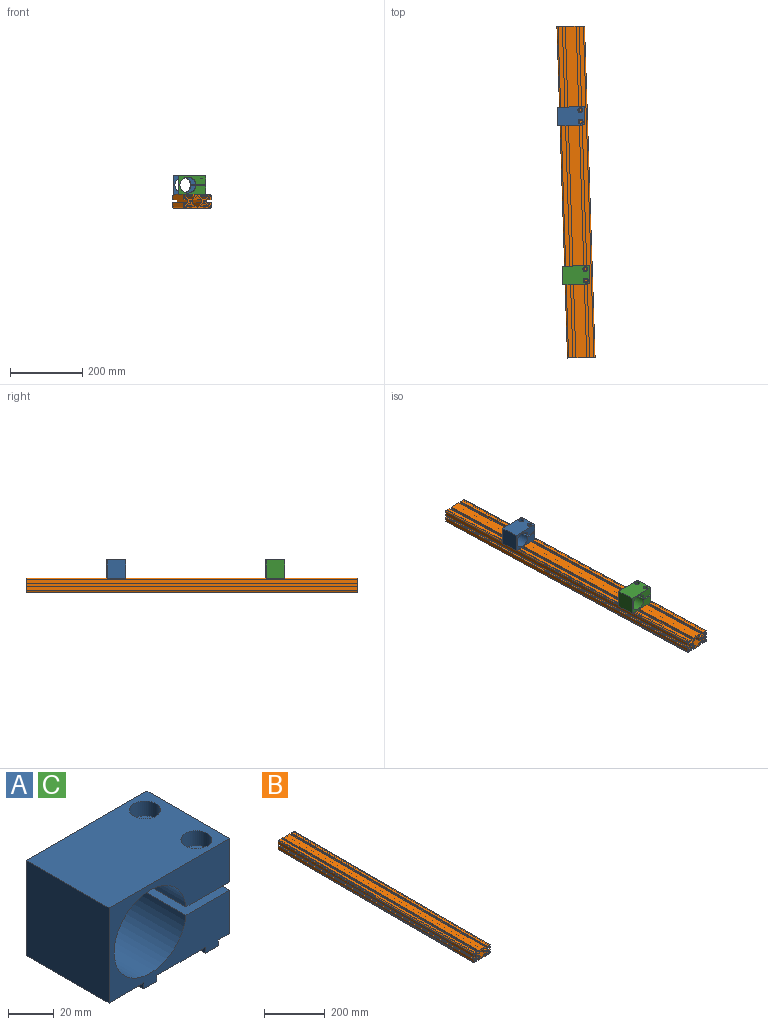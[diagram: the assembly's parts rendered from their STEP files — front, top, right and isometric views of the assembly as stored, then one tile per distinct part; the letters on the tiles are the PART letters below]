
ASSEMBLY  parts=3 mates=4
PART A: 32 faces, bbox 74.3x50.8x54 mm
  f0: plane 29.16x3.18mm, normal (-1,0,0), area 92.6mm2, adj f4,f13,f30,f31
  f1: plane 8.23x3.18mm, normal (-1,0,0), area 26.1mm2, adj f3,f13,f23,f31
  f2: plane 8.23x3.18mm, normal (-1,0,0), area 26.1mm2, adj f13,f14,f22,f30
  f3: plane 8.23x8.03mm, normal (0,0,-1), area 48.9mm2, adj f1,f5,f23,f31
  f4: plane 29.16x8.03mm, normal (0,0,-1), area 199.7mm2, adj f0,f6,f30,f31
  f5: plane 8.23x3.18mm, normal (1,0,0), area 26.1mm2, adj f3,f15,f23,f31
  f6: plane 29.16x3.18mm, normal (1,0,0), area 92.6mm2, adj f4,f15,f30,f31
  f7: plane 8.23x3.18mm, normal (1,0,0), area 26.1mm2, adj f14,f15,f22,f30
  f8: plane 50.8x50.8mm, normal (-1,0,0), area 2580.6mm2, adj f9,f21,f22,f23
  f9: plane 50.8x21.39mm, normal (0,0,-1), area 1086.4mm2, adj f8,f10,f22,f23
  f10: plane 50.8x3.18mm, normal (-1,0,0), area 161.3mm2, adj f9,f11,f22,f23
  f11: plane 50.8x8.03mm, normal (0,0,-1), area 407.7mm2, adj f10,f12,f22,f23
  f12: plane 50.8x3.18mm, normal (1,0,0), area 161.3mm2, adj f11,f13,f22,f23
  f13: plane 50.8x30.07mm, normal (0,0,-1), area 1527mm2, adj f0,f1,f2,f12,f22,f23,f30,f31
  f14: plane 8.23x8.03mm, normal (0,0,-1), area 48.9mm2, adj f2,f7,f22,f30
  f15: plane 50.8x6.74mm, normal (0,0,-1), area 341.6mm2, adj f5,f6,f7,f16,f22,f23,f30,f31
  f16: plane 50.8x23.18mm, normal (1,0,0), area 1177.4mm2, adj f15,f17,f22,f23
  f17: plane 50.8x26.74mm, normal (0,0,1), area 1246.5mm2, adj f16,f18,f22,f23,f30,f31
  f18: cylinder r=22.23mm len=50.8mm, axis (0,-1,0), area 6867.7mm2, adj f17,f19,f22,f23
  f19: plane 50.8x26.74mm, normal (0,0,-1), area 1246.5mm2, adj f18,f20,f22,f23,f24,f27
  f20: plane 50.8x23.18mm, normal (1,0,0), area 1177.4mm2, adj f19,f21,f22,f23
  f21: plane 74.25x50.8mm, normal (0,0,1), area 3485.9mm2, adj f8,f20,f22,f23,f26,f29
  f22: plane 74.25x53.98mm, normal (0,1,0), area 2152.6mm2, adj f2,f7,f8,f9,f10,f11,f12,f13
  f23: plane 74.25x53.98mm, normal (0,-1,0), area 2152.6mm2, adj f1,f3,f5,f8,f9,f10,f11,f12
  f24: cylinder r=4.22mm len=15.24mm, axis (0,0,1), area 403.7mm2, adj f19,f25
  f25: plane 13.49x13.49mm, normal (0,0,1), area 87.2mm2, adj f24,f26
  f26: cylinder r=6.75mm len=13.49mm, axis (0,0,1), area 336.5mm2, adj f21,f25
  f27: cylinder r=4.22mm len=15.24mm, axis (0,0,1), area 403.7mm2, adj f19,f28
  f28: plane 13.49x13.49mm, normal (0,0,1), area 87.2mm2, adj f27,f29
  f29: cylinder r=6.75mm len=13.49mm, axis (0,0,1), area 336.5mm2, adj f21,f28
  f30: cylinder r=4.22mm len=26.35mm, axis (0,0,1), area 681.4mm2, adj f0,f2,f4,f6,f7,f13,f14,f15
  f31: cylinder r=4.22mm len=26.35mm, axis (0,0,1), area 681.4mm2, adj f0,f1,f3,f4,f5,f6,f13,f15
PART B: 122 faces, bbox 76.2x914.4x38.1 mm
  f0: plane 76.2x38.1mm, normal (0,-1,0), area 1182.5mm2, adj f2,f3,f4,f5,f6,f7,f8,f9
  f1: plane 76.2x38.1mm, normal (0,1,0), area 1182.5mm2, adj f2,f3,f4,f5,f6,f7,f8,f9
  f2: plane 914.4x5.71mm, normal (0.71,0,0.71), area 7385.6mm2, adj f0,f1,f3,f93
  f3: plane 914.4x3.23mm, normal (1,0,0), area 2953.1mm2, adj f0,f1,f2,f4
  f4: plane 914.4x3.43mm, normal (0,0,-1), area 3135.5mm2, adj f0,f1,f3,f5
  f5: plane 914.4x1.17mm, normal (-1,0,0), area 1068.4mm2, adj f0,f1,f4,f6
  f6: plane 914.4x2.79mm, normal (0,0,-1), area 2554.8mm2, adj f0,f1,f5,f7
  f7: plane 914.4x4.55mm, normal (1,0,0), area 4157.4mm2, adj f0,f1,f6,f8
  f8: plane 914.4x11.94mm, normal (0,0,1), area 10916.1mm2, adj f0,f1,f7,f9
  f9: cylinder r=3.05mm len=914.4mm, axis (0,1,0), area 4378mm2, adj f0,f1,f8,f10
  f10: plane 914.4x11.94mm, normal (-1,0,0), area 10916.1mm2, adj f0,f1,f9,f11
  f11: plane 914.4x4.55mm, normal (0,0,-1), area 4157.4mm2, adj f0,f1,f10,f12
  f12: plane 914.4x2.79mm, normal (1,0,0), area 2554.8mm2, adj f0,f1,f11,f13
  f13: plane 914.4x1.17mm, normal (0,0,1), area 1068.4mm2, adj f0,f1,f12,f14
  f14: plane 914.4x3.43mm, normal (1,0,0), area 3135.5mm2, adj f0,f1,f13,f15
  f15: plane 914.4x3.23mm, normal (0,0,-1), area 2953.1mm2, adj f0,f1,f14,f16
  f16: plane 914.4x5.71mm, normal (-0.71,0,-0.71), area 7385.6mm2, adj f0,f1,f15,f17
  f17: plane 914.4x9.15mm, normal (-1,0,0), area 8368.1mm2, adj f0,f1,f16,f18
  f18: plane 914.4x5.71mm, normal (-0.71,0,0.71), area 7385.6mm2, adj f0,f1,f17,f19
  f19: plane 914.4x3.23mm, normal (0,0,1), area 2953.1mm2, adj f0,f1,f18,f20
  f20: plane 914.4x3.43mm, normal (1,0,0), area 3135.5mm2, adj f0,f1,f19,f21
  f21: plane 914.4x1.17mm, normal (0,0,-1), area 1068.4mm2, adj f0,f1,f20,f22
  f22: plane 914.4x2.79mm, normal (1,0,0), area 2554.8mm2, adj f0,f1,f21,f23
  f23: plane 914.4x4.55mm, normal (0,0,1), area 4157.4mm2, adj f0,f1,f22,f24
  f24: plane 914.4x11.94mm, normal (-1,0,0), area 10916.1mm2, adj f0,f1,f23,f25
  f25: cylinder r=3.05mm len=914.4mm, axis (0,1,0), area 4378mm2, adj f0,f1,f24,f26
  f26: plane 914.4x11.94mm, normal (0,0,-1), area 10916.1mm2, adj f0,f1,f25,f27
  f27: plane 914.4x4.55mm, normal (1,0,0), area 4157.4mm2, adj f0,f1,f26,f28
  f28: plane 914.4x2.79mm, normal (0,0,1), area 2554.8mm2, adj f0,f1,f27,f29
  f29: plane 914.4x1.17mm, normal (-1,0,0), area 1068.4mm2, adj f0,f1,f28,f30
  f30: plane 914.4x3.43mm, normal (0,0,1), area 3135.5mm2, adj f0,f1,f29,f31
  f31: plane 914.4x3.23mm, normal (1,0,0), area 2953.1mm2, adj f0,f1,f30,f32
  f32: plane 914.4x5.71mm, normal (0.71,0,-0.71), area 7385.6mm2, adj f0,f1,f31,f33
  f33: plane 914.4x9.15mm, normal (0,0,-1), area 8368.1mm2, adj f0,f1,f32,f34
  f34: plane 914.4x5.71mm, normal (-0.71,0,-0.71), area 7385.6mm2, adj f0,f1,f33,f35
  f35: plane 914.4x3.23mm, normal (-1,0,0), area 2953.1mm2, adj f0,f1,f34,f36
  f36: plane 914.4x3.43mm, normal (0,0,1), area 3135.5mm2, adj f0,f1,f35,f37
  f37: plane 914.4x1.17mm, normal (1,0,0), area 1068.4mm2, adj f0,f1,f36,f38
  f38: plane 914.4x2.79mm, normal (0,0,1), area 2554.8mm2, adj f0,f1,f37,f39
  f39: plane 914.4x4.55mm, normal (-1,0,0), area 4157.4mm2, adj f0,f1,f38,f40
  f40: plane 914.4x29.97mm, normal (0,0,-1), area 27406.4mm2, adj f0,f1,f39,f41
  f41: plane 914.4x4.55mm, normal (1,0,0), area 4157.4mm2, adj f0,f1,f40,f42
  f42: plane 914.4x2.79mm, normal (0,0,1), area 2554.8mm2, adj f0,f1,f41,f43
  f43: plane 914.4x1.17mm, normal (-1,0,0), area 1068.4mm2, adj f0,f1,f42,f44
  f44: plane 914.4x3.43mm, normal (0,0,1), area 3135.5mm2, adj f0,f1,f43,f45
  f45: plane 914.4x3.23mm, normal (1,0,0), area 2953.1mm2, adj f0,f1,f44,f46
  f46: plane 914.4x5.71mm, normal (0.71,0,-0.71), area 7385.6mm2, adj f0,f1,f45,f47
  f47: plane 914.4x9.15mm, normal (0,0,-1), area 8368.1mm2, adj f0,f1,f46,f48
  f48: plane 914.4x5.71mm, normal (-0.71,0,-0.71), area 7385.6mm2, adj f0,f1,f47,f49
  f49: plane 914.4x3.23mm, normal (-1,0,0), area 2953.1mm2, adj f0,f1,f48,f50
  f50: plane 914.4x3.43mm, normal (0,0,1), area 3135.5mm2, adj f0,f1,f49,f51
  f51: plane 914.4x1.17mm, normal (1,0,0), area 1068.4mm2, adj f0,f1,f50,f52
  f52: plane 914.4x2.79mm, normal (0,0,1), area 2554.8mm2, adj f0,f1,f51,f53
  f53: plane 914.4x4.55mm, normal (-1,0,0), area 4157.4mm2, adj f0,f1,f52,f54
  f54: plane 914.4x11.94mm, normal (0,0,-1), area 10916.1mm2, adj f0,f1,f53,f55
  f55: cylinder r=3.05mm len=914.4mm, axis (0,1,0), area 4378mm2, adj f0,f1,f54,f56
  f56: plane 914.4x11.94mm, normal (1,0,0), area 10916.1mm2, adj f0,f1,f55,f57
  f57: plane 914.4x4.55mm, normal (0,0,1), area 4157.4mm2, adj f0,f1,f56,f58
  f58: plane 914.4x2.79mm, normal (-1,0,0), area 2554.8mm2, adj f0,f1,f57,f59
  f59: plane 914.4x1.17mm, normal (0,0,-1), area 1068.4mm2, adj f0,f1,f58,f60
  f60: plane 914.4x3.43mm, normal (-1,0,0), area 3135.5mm2, adj f0,f1,f59,f61
  f61: plane 914.4x3.23mm, normal (0,0,1), area 2953.1mm2, adj f0,f1,f60,f62
  f62: plane 914.4x5.71mm, normal (0.71,0,0.71), area 7385.6mm2, adj f0,f1,f61,f63
  f63: plane 914.4x9.15mm, normal (1,0,0), area 8368.1mm2, adj f0,f1,f62,f64
  f64: plane 914.4x5.71mm, normal (0.71,0,-0.71), area 7385.6mm2, adj f0,f1,f63,f65
  f65: plane 914.4x3.23mm, normal (0,0,-1), area 2953.1mm2, adj f0,f1,f64,f66
  f66: plane 914.4x3.43mm, normal (-1,0,0), area 3135.5mm2, adj f0,f1,f65,f67
  f67: plane 914.4x1.17mm, normal (0,0,1), area 1068.4mm2, adj f0,f1,f66,f68
  f68: plane 914.4x2.79mm, normal (-1,0,0), area 2554.8mm2, adj f0,f1,f67,f69
  f69: plane 914.4x4.55mm, normal (0,0,-1), area 4157.4mm2, adj f0,f1,f68,f70
  f70: plane 914.4x11.94mm, normal (1,0,0), area 10916.1mm2, adj f0,f1,f69,f71
  f71: cylinder r=3.05mm len=914.4mm, axis (0,1,0), area 4378mm2, adj f0,f1,f70,f72
  f72: plane 914.4x11.94mm, normal (0,0,1), area 10916.1mm2, adj f0,f1,f71,f73
  f73: plane 914.4x4.55mm, normal (-1,0,0), area 4157.4mm2, adj f0,f1,f72,f74
  f74: plane 914.4x2.79mm, normal (0,0,-1), area 2554.8mm2, adj f0,f1,f73,f75
  f75: plane 914.4x1.17mm, normal (1,0,0), area 1068.4mm2, adj f0,f1,f74,f76
  f76: plane 914.4x3.43mm, normal (0,0,-1), area 3135.5mm2, adj f0,f1,f75,f77
  f77: plane 914.4x3.23mm, normal (-1,0,0), area 2953.1mm2, adj f0,f1,f76,f78
  f78: plane 914.4x5.71mm, normal (-0.71,0,0.71), area 7385.6mm2, adj f0,f1,f77,f79
  f79: plane 914.4x9.15mm, normal (0,0,1), area 8368.1mm2, adj f0,f1,f78,f80
  f80: plane 914.4x5.71mm, normal (0.71,0,0.71), area 7385.6mm2, adj f0,f1,f79,f81
  f81: plane 914.4x3.23mm, normal (1,0,0), area 2953.1mm2, adj f0,f1,f80,f82
  f82: plane 914.4x3.43mm, normal (0,0,-1), area 3135.5mm2, adj f0,f1,f81,f83
  f83: plane 914.4x1.17mm, normal (-1,0,0), area 1068.4mm2, adj f0,f1,f82,f84
  f84: plane 914.4x2.79mm, normal (0,0,-1), area 2554.8mm2, adj f0,f1,f83,f85
  f85: plane 914.4x4.55mm, normal (1,0,0), area 4157.4mm2, adj f0,f1,f84,f86
  f86: plane 914.4x29.97mm, normal (0,0,1), area 27406.4mm2, adj f0,f1,f85,f87
  f87: plane 914.4x4.55mm, normal (-1,0,0), area 4157.4mm2, adj f0,f1,f86,f88
  f88: plane 914.4x2.79mm, normal (0,0,-1), area 2554.8mm2, adj f0,f1,f87,f89
  f89: plane 914.4x1.17mm, normal (1,0,0), area 1068.4mm2, adj f0,f1,f88,f90
  f90: plane 914.4x3.43mm, normal (0,0,-1), area 3135.5mm2, adj f0,f1,f89,f91
  f91: plane 914.4x3.23mm, normal (-1,0,0), area 2953.1mm2, adj f0,f1,f90,f92
  f92: plane 914.4x5.71mm, normal (-0.71,0,0.71), area 7385.6mm2, adj f0,f1,f91,f93
  f93: plane 914.4x9.15mm, normal (0,0,1), area 8368.1mm2, adj f0,f1,f2,f92
  f94: plane 914.4x12.32mm, normal (0.71,0,0.71), area 15930.4mm2, adj f0,f1,f95,f99
  f95: plane 914.4x12.32mm, normal (-0.71,0,0.71), area 15930.4mm2, adj f0,f1,f94,f96
  f96: plane 914.4x9.15mm, normal (-1,0,0), area 8368.1mm2, adj f0,f1,f95,f97
  f97: plane 914.4x12.32mm, normal (-0.71,0,-0.71), area 15930.4mm2, adj f0,f1,f96,f98
  f98: plane 914.4x12.32mm, normal (0.71,0,-0.71), area 15930.4mm2, adj f0,f1,f97,f99
  f99: plane 914.4x9.15mm, normal (1,0,0), area 8368.1mm2, adj f0,f1,f94,f98
  f100: cylinder r=2.55mm len=914.4mm, axis (0,1,0), area 14666.1mm2, adj f0,f1
  f101: cylinder r=2.55mm len=914.4mm, axis (0,1,0), area 14666.1mm2, adj f0,f1
  f102: plane 914.4x2.59mm, normal (0,0,-1), area 2369mm2, adj f0,f1,f103,f106
  f103: cylinder r=2.79mm len=914.4mm, axis (0,1,0), area 4013.1mm2, adj f0,f1,f102,f104
  f104: plane 914.4x2.59mm, normal (1,0,0), area 2369mm2, adj f0,f1,f103,f105
  f105: plane 914.4x5.39mm, normal (0,0,1), area 4923.9mm2, adj f0,f1,f104,f106
  f106: plane 914.4x5.38mm, normal (-1,0,0), area 4923.9mm2, adj f0,f1,f102,f105
  f107: plane 914.4x5.39mm, normal (0,0,-1), area 4923.9mm2, adj f0,f1,f108,f111
  f108: plane 914.4x2.59mm, normal (1,0,0), area 2369mm2, adj f0,f1,f107,f109
  f109: cylinder r=2.79mm len=914.4mm, axis (0,1,0), area 4013.1mm2, adj f0,f1,f108,f110
  f110: plane 914.4x2.59mm, normal (0,0,1), area 2369mm2, adj f0,f1,f109,f111
  f111: plane 914.4x5.38mm, normal (-1,0,0), area 4923.9mm2, adj f0,f1,f107,f110
  f112: plane 914.4x5.38mm, normal (1,0,0), area 4923.9mm2, adj f0,f1,f113,f116
  f113: plane 914.4x2.59mm, normal (0,0,1), area 2369mm2, adj f0,f1,f112,f114
  f114: cylinder r=2.79mm len=914.4mm, axis (0,1,0), area 4013.1mm2, adj f0,f1,f113,f115
  f115: plane 914.4x2.59mm, normal (-1,0,0), area 2369mm2, adj f0,f1,f114,f116
  f116: plane 914.4x5.39mm, normal (0,0,-1), area 4923.9mm2, adj f0,f1,f112,f115
  f117: plane 914.4x5.39mm, normal (0,0,1), area 4923.9mm2, adj f0,f1,f118,f121
  f118: plane 914.4x2.59mm, normal (-1,0,0), area 2369mm2, adj f0,f1,f117,f119
  f119: cylinder r=2.79mm len=914.4mm, axis (0,1,0), area 4013.1mm2, adj f0,f1,f118,f120
  f120: plane 914.4x2.59mm, normal (0,0,-1), area 2369mm2, adj f0,f1,f119,f121
  f121: plane 914.4x5.38mm, normal (1,0,0), area 4923.9mm2, adj f0,f1,f117,f120
PART C: same geometry as A
PLACE A rot(axis=(0,0,1),1.8deg) t=(60.35,677.39,-380.52)mm
PLACE B rot(axis=(0,0,-1),178.2deg) t=(80.87,36.3,-380.52)mm
PLACE C rot(axis=(0,0,1),1.8deg) t=(74.36,238.54,-380.52)mm
MATE cylindrical A.f18 <-> C.f18  axis (0.03,-1,0) through (55.09,245.2,-336.07)mm
MATE planar A.f13 <-> B.f86  axis (0,0,-1) through (74.12,245.81,-361.47)mm
MATE planar C.f10 <-> B.f73  axis (-1,-0.03,0) through (65.09,-193.77,-363.06)mm
MATE planar C.f13 <-> B.f86  axis (0,0,-1) through (103.17,-192.56,-361.47)mm
